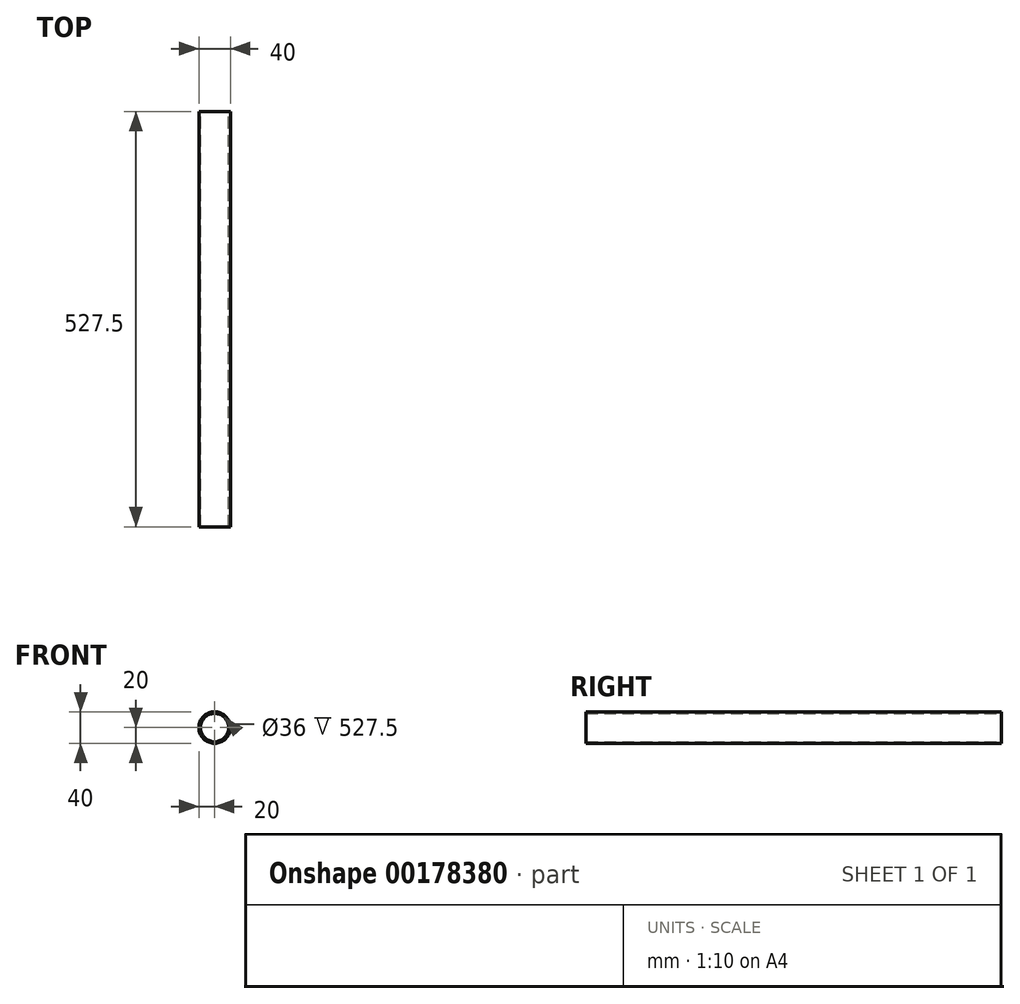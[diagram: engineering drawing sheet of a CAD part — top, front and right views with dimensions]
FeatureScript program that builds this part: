
annotation { "Feature Type Name" : "Feature", "Feature Type Description" : "" }
export const myFeature = defineFeature(function(context is Context, id is Id, definition is map)
    precondition{}
    {
        {
            var Q0;
            Q0=qCreatedBy(makeId("Front.planeOp"),FACE);
            var sketch = newSketch(context, id + "F0", { "sketchPlane" : qUnion([Q0])});
            skCircle(sketch, "E0", {"center": v(0, 0) * mm, "radius": 20 * mm});
            skCircle(sketch, "E1.0", {"center": v(0, 0) * mm, "radius": 18 * mm});
            skSolve(sketch);
        }
        {
            var Q0;
            Q0=makeQuery(id+"F0.imprint","IMPRINT",FACE,{"disambiguationData":[TD([[makeQuery(id+"F0.imprint","IMPRINT",EDGE,{"derivedFrom":sQuery(id+"F0.wireOp",EDGE,"E0")}),1.0]])]});
            extrude(context, id + "F1", {"entities" : qUnion([Q0]), "depth" : 527.5 * mm});
        }
    });
